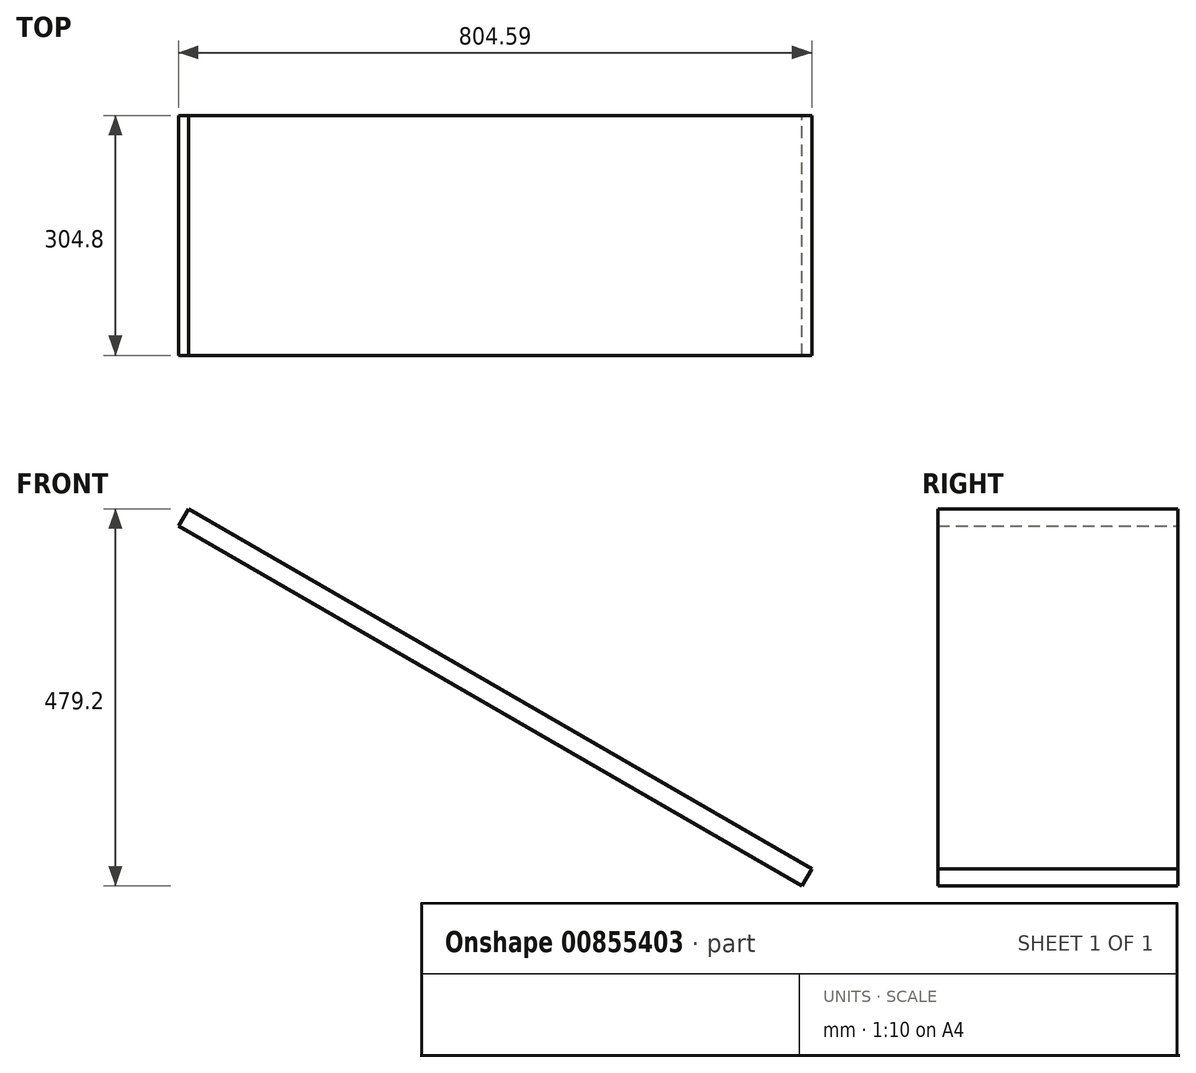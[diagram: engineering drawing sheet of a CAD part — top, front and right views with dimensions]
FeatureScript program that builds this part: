
annotation { "Feature Type Name" : "Feature", "Feature Type Description" : "" }
export const myFeature = defineFeature(function(context is Context, id is Id, definition is map)
    precondition{}
    {
        {
            var Q0;
            Q0=qCreatedBy(makeId("Front.planeOp"),FACE);
            var sketch = newSketch(context, id + "F0", { "sketchPlane" : qUnion([Q0])});
            skLineSegment(sketch, "E0", {"start": v(0, 0) * mm, "end": v(0, -457.2) * mm, "construction": true});
            skLineSegment(sketch, "E1", {"start": v(0, 0) * mm, "end": v(791.9, -457.2) * mm});
            skLineSegment(sketch, "E2.0", {"start": v(12.7, 22) * mm, "end": v(804.6, -435.2) * mm});
            skLineSegment(sketch, "E3", {"start": v(791.9, -457.2) * mm, "end": v(804.6, -435.2) * mm});
            skLineSegment(sketch, "E4", {"start": v(12.7, 22) * mm, "end": v(0, 0) * mm});
            skSolve(sketch);
        }
        {
            var Q0;
            Q0 = qSketchRegion(id + "F0", true);
            extrude(context, id + "F1", {"entities" : qUnion([Q0]), "endBound" : BoundingType.SYMMETRIC, "depth" : 304.8 * mm, "offsetDistance" : 25.4 * mm});
        }
    });
